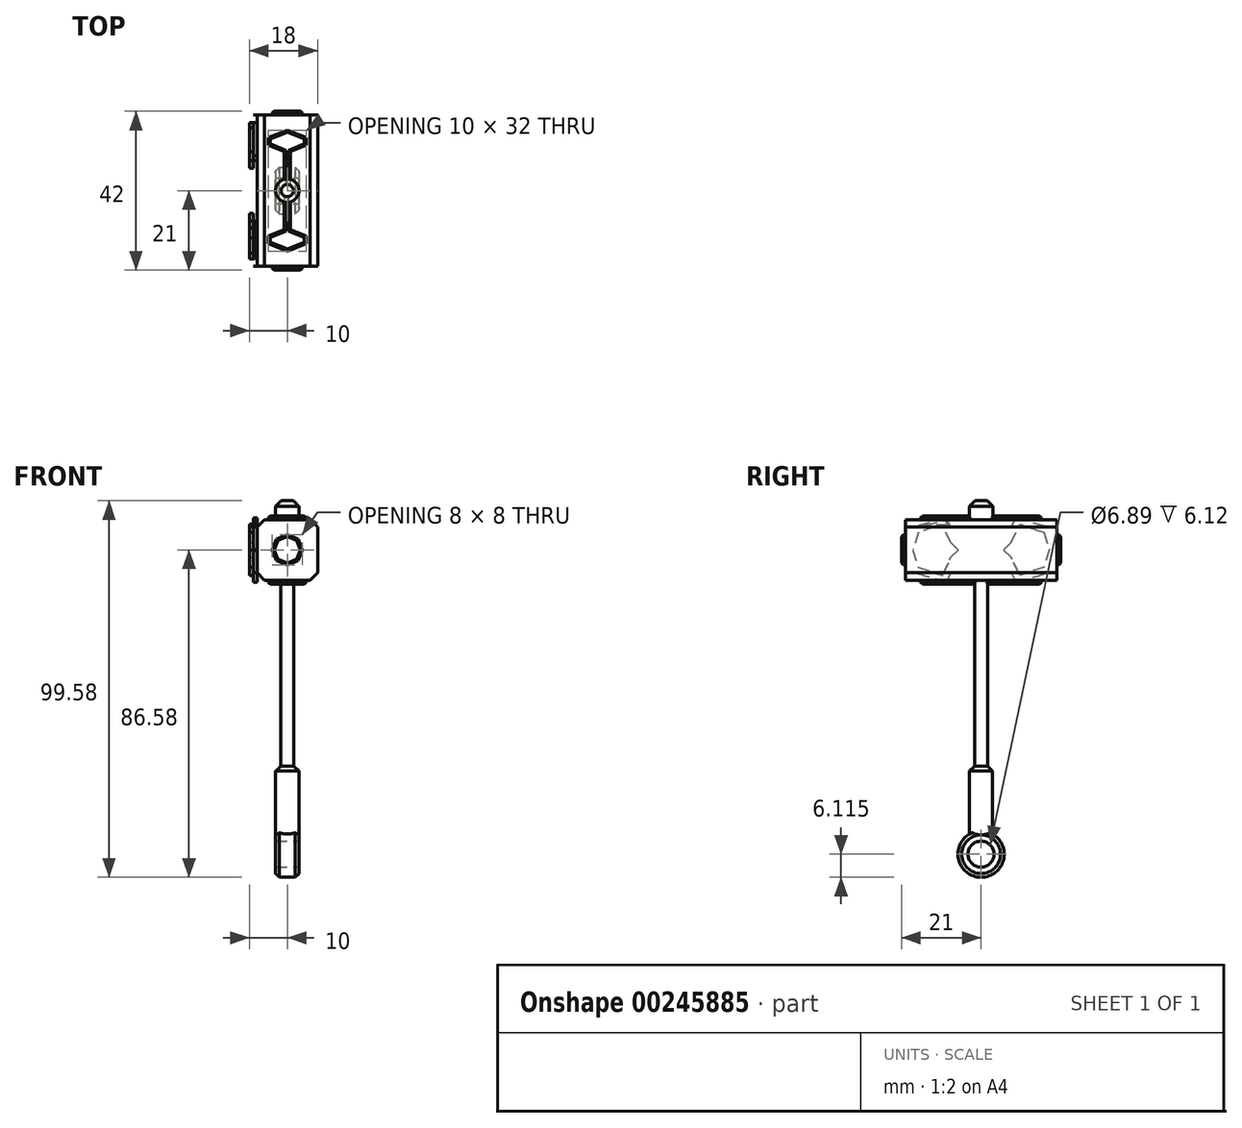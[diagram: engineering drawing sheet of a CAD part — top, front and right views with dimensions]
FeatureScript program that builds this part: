
annotation { "Feature Type Name" : "Feature", "Feature Type Description" : "" }
export const myFeature = defineFeature(function(context is Context, id is Id, definition is map)
    precondition{}
    {
        {
            var Q0;
            Q0=qCreatedBy(makeId("Right.planeOp"),FACE);
            var sketch = newSketch(context, id + "F0", { "sketchPlane" : qUnion([Q0])});
            skLineSegment(sketch, "E0", {"start": v(0, 0) * mm, "end": v(25, 0) * mm});
            skLineSegment(sketch, "E1", {"start": v(25, 0) * mm, "end": v(25, 8) * mm});
            skLineSegment(sketch, "E2", {"start": v(25, 8) * mm, "end": v(0, 8) * mm});
            skLineSegment(sketch, "E3", {"start": v(0, 8) * mm, "end": v(-25, 8) * mm});
            skLineSegment(sketch, "E4", {"start": v(-25, 8) * mm, "end": v(-25, 0) * mm});
            skLineSegment(sketch, "E5", {"start": v(-25, 0) * mm, "end": v(0, 0) * mm});
            skLineSegment(sketch, "E6", {"start": v(25, 0) * mm, "end": v(25, -8) * mm});
            skLineSegment(sketch, "E7", {"start": v(25, -8) * mm, "end": v(-25, -8) * mm});
            skLineSegment(sketch, "E8", {"start": v(-25, -8) * mm, "end": v(-25, 0) * mm});
            skSolve(sketch);
        }
        {
            var Q0;
            Q0=makeQuery(id+"F0.imprint","IMPRINT",FACE,{"disambiguationData":[TD([[makeQuery(id+"F0.imprint","IMPRINT",EDGE,{"derivedFrom":sQuery(id+"F0.wireOp",EDGE,"E0")}),1.0]])]});
            var Q1;
            Q1=makeQuery(id+"F0.imprint","IMPRINT",FACE,{"disambiguationData":[TD([[makeQuery(id+"F0.imprint","IMPRINT",EDGE,{"derivedFrom":sQuery(id+"F0.wireOp",EDGE,"E0")}),-1.0]])]});
            extrude(context, id + "F1", {"entities" : qUnion([Q0, Q1]), "oppositeDirection" : true, "depth" : 8 * mm});
        }
        {
            var Q0;
            Q0=makeQuery(id+"F1.opExtrude","CAP_FACE",FACE,{"disambiguationData":[OSD([sQuery(id+"F0.wireOp",EDGE,"E1"),sQuery(id+"F0.wireOp",EDGE,"E2"),sQuery(id+"F0.wireOp",EDGE,"E3"),sQuery(id+"F0.wireOp",EDGE,"E4"),sQuery(id+"F0.wireOp",EDGE,"E6"),sQuery(id+"F0.wireOp",EDGE,"E7"),sQuery(id+"F0.wireOp",EDGE,"E8")])],"isStart":true});
            extrude(context, id + "F2", {"entities" : qUnion([Q0]), "operationType" : NewBodyOperationType.ADD, "depth" : 8 * mm});
        }
        {
            var Q0;
            {var subQ0=sQuery(id+"F0.wireOp",EDGE,"E8");var subQ1=sQuery(id+"F0.wireOp",EDGE,"E4");Q0=makeQuery(id+"F2.boolean.opBoolean","MERGE",FACE,{"derivedFrom":[makeQuery(id+"F1.opExtrude","SWEPT_FACE",FACE,{"disambiguationData":[OSD([subQ1,subQ0])]}),makeQuery(id+"F2.opExtrude","SWEPT_FACE",FACE,{"disambiguationData":[OSD([subQ1,subQ0])]})]});}
            extrude(context, id + "F3", {"entities" : qUnion([Q0]), "operationType" : NewBodyOperationType.REMOVE, "oppositeDirection" : true, "depth" : 5 * mm});
        }
        {
            var Q0;
            {var subQ0=sQuery(id+"F0.wireOp",EDGE,"E6");var subQ1=sQuery(id+"F0.wireOp",EDGE,"E1");Q0=makeQuery(id+"F2.boolean.opBoolean","MERGE",FACE,{"derivedFrom":[makeQuery(id+"F1.opExtrude","SWEPT_FACE",FACE,{"disambiguationData":[OSD([subQ1,subQ0])]}),makeQuery(id+"F2.opExtrude","SWEPT_FACE",FACE,{"disambiguationData":[OSD([subQ1,subQ0])]})]});}
            extrude(context, id + "F4", {"entities" : qUnion([Q0]), "operationType" : NewBodyOperationType.REMOVE, "oppositeDirection" : true, "depth" : 5 * mm});
        }
        {
            var Q0;
            Q0=makeQuery(id+"F1.opExtrude","CAP_EDGE",EDGE,{"disambiguationData":[OSD([sQuery(id+"F0.wireOp",EDGE,"E2"),sQuery(id+"F0.wireOp",EDGE,"E3")])],"isStart":false});
            var Q1;
            Q1=makeQuery(id+"F4.boolean.opBoolean","COPY",EDGE,{"derivedFrom":makeQuery(id+"F4.opExtrude","CAP_EDGE",EDGE,{"disambiguationData":[OSD([sQuery(id+"F0.wireOp",EDGE,"E1"),sQuery(id+"F0.wireOp",EDGE,"E2")])],"isStart":false})});
            var Q2;
            {var subQ0=sQuery(id+"F0.wireOp",EDGE,"E6");var subQ1=sQuery(id+"F0.wireOp",EDGE,"E1");Q2=makeQuery(id+"F4.boolean.opBoolean","COPY",EDGE,{"derivedFrom":makeQuery(id+"F4.opExtrude","CAP_EDGE",EDGE,{"disambiguationData":[OSD([subQ1,subQ0]),TDD([makeQuery(id+"F1.opExtrude","CAP_EDGE",EDGE,{"disambiguationData":[OSD([subQ1,subQ0])],"isStart":false})])],"isStart":false})});}
            var Q3;
            Q3=makeQuery(id+"F1.opExtrude","CAP_EDGE",EDGE,{"disambiguationData":[OSD([sQuery(id+"F0.wireOp",EDGE,"E7")])],"isStart":false});
            var Q4;
            {var subQ0=sQuery(id+"F0.wireOp",EDGE,"E8");var subQ1=sQuery(id+"F0.wireOp",EDGE,"E4");Q4=makeQuery(id+"F3.boolean.opBoolean","COPY",EDGE,{"derivedFrom":makeQuery(id+"F3.opExtrude","CAP_EDGE",EDGE,{"disambiguationData":[OSD([subQ1,subQ0]),TDD([makeQuery(id+"F1.opExtrude","CAP_EDGE",EDGE,{"disambiguationData":[OSD([subQ1,subQ0])],"isStart":false})])],"isStart":false})});}
            var Q5;
            {var subQ0=sQuery(id+"F0.wireOp",EDGE,"E8");var subQ1=sQuery(id+"F0.wireOp",EDGE,"E4");Q5=makeQuery(id+"F3.boolean.opBoolean","COPY",EDGE,{"derivedFrom":makeQuery(id+"F3.opExtrude","CAP_EDGE",EDGE,{"disambiguationData":[OSD([subQ1,subQ0]),TDD([makeQuery(id+"F2.opExtrude","CAP_EDGE",EDGE,{"disambiguationData":[OSD([subQ1,subQ0])],"isStart":false})])],"isStart":false})});}
            var Q6;
            Q6=makeQuery(id+"F3.boolean.opBoolean","COPY",EDGE,{"derivedFrom":makeQuery(id+"F3.opExtrude","CAP_EDGE",EDGE,{"disambiguationData":[OSD([sQuery(id+"F0.wireOp",EDGE,"E3"),sQuery(id+"F0.wireOp",EDGE,"E4")])],"isStart":false})});
            var Q7;
            Q7=makeQuery(id+"F3.boolean.opBoolean","COPY",EDGE,{"derivedFrom":makeQuery(id+"F3.opExtrude","CAP_EDGE",EDGE,{"disambiguationData":[OSD([sQuery(id+"F0.wireOp",EDGE,"E7"),sQuery(id+"F0.wireOp",EDGE,"E8")])],"isStart":false})});
            var Q8;
            Q8=makeQuery(id+"F2.opExtrude","CAP_EDGE",EDGE,{"disambiguationData":[OSD([sQuery(id+"F0.wireOp",EDGE,"E2"),sQuery(id+"F0.wireOp",EDGE,"E3")])],"isStart":false});
            var Q9;
            Q9=makeQuery(id+"F2.opExtrude","CAP_EDGE",EDGE,{"disambiguationData":[OSD([sQuery(id+"F0.wireOp",EDGE,"E7")])],"isStart":false});
            var Q10;
            Q10=makeQuery(id+"F4.boolean.opBoolean","COPY",EDGE,{"derivedFrom":makeQuery(id+"F4.opExtrude","CAP_EDGE",EDGE,{"disambiguationData":[OSD([sQuery(id+"F0.wireOp",EDGE,"E6"),sQuery(id+"F0.wireOp",EDGE,"E7")])],"isStart":false})});
            var Q11;
            {var subQ0=sQuery(id+"F0.wireOp",EDGE,"E6");var subQ1=sQuery(id+"F0.wireOp",EDGE,"E1");Q11=makeQuery(id+"F4.boolean.opBoolean","COPY",EDGE,{"derivedFrom":makeQuery(id+"F4.opExtrude","CAP_EDGE",EDGE,{"disambiguationData":[OSD([subQ1,subQ0]),TDD([makeQuery(id+"F2.opExtrude","CAP_EDGE",EDGE,{"disambiguationData":[OSD([subQ1,subQ0])],"isStart":false})])],"isStart":false})});}
            chamfer(context, id + "F5", {"entities" : qUnion([Q0, Q1, Q2, Q3, Q4, Q5, Q6, Q7, Q8, Q9, Q10, Q11]), "width" : 2 * mm, "tangentPropagation" : true});
        }
        {
            var Q0;
            {var subQ0=sQuery(id+"F0.wireOp",EDGE,"E3");var subQ1=sQuery(id+"F0.wireOp",EDGE,"E2");Q0=makeQuery(id+"F2.boolean.opBoolean","MERGE",FACE,{"derivedFrom":[makeQuery(id+"F1.opExtrude","SWEPT_FACE",FACE,{"disambiguationData":[OSD([subQ1,subQ0])]}),makeQuery(id+"F2.opExtrude","SWEPT_FACE",FACE,{"disambiguationData":[OSD([subQ1,subQ0])]})]});}
            var sketch = newSketch(context, id + "F6", { "sketchPlane" : qUnion([Q0])});
            skCircle(sketch, "E9", {"center": v(0, 0) * mm, "radius": 1.75 * mm});
            skSolve(sketch);
        }
        {
            var Q0;
            Q0=makeQuery(id+"F6.imprint","IMPRINT",FACE,{"disambiguationData":[TD([[makeQuery(id+"F6.imprint","IMPRINT",EDGE,{"derivedFrom":sQuery(id+"F6.wireOp",EDGE,"E9")}),1.0]])]});
            extrude(context, id + "F7", {"entities" : qUnion([Q0]), "operationType" : NewBodyOperationType.ADD, "oppositeDirection" : true, "depth" : 70 * mm});
        }
        {
            var Q0;
            Q0=makeQuery(id+"F6.imprint","IMPRINT",FACE,{"disambiguationData":[TD([[makeQuery(id+"F6.imprint","IMPRINT",EDGE,{"derivedFrom":sQuery(id+"F6.wireOp",EDGE,"E9")}),1.0]])]});
            extrude(context, id + "F8", {"entities" : qUnion([Q0]), "operationType" : NewBodyOperationType.ADD, "depth" : 5 * mm});
        }
        {
            var Q0;
            Q0=makeQuery(id+"F1.opExtrude","CAP_FACE",FACE,{"disambiguationData":[OSD([sQuery(id+"F0.wireOp",EDGE,"E1"),sQuery(id+"F0.wireOp",EDGE,"E2"),sQuery(id+"F0.wireOp",EDGE,"E3"),sQuery(id+"F0.wireOp",EDGE,"E4"),sQuery(id+"F0.wireOp",EDGE,"E6"),sQuery(id+"F0.wireOp",EDGE,"E7"),sQuery(id+"F0.wireOp",EDGE,"E8")])],"isStart":false});
            var sketch = newSketch(context, id + "F9", { "sketchPlane" : qUnion([Q0])});
            skLineSegment(sketch, "E10", {"start": v(0, 0) * mm, "end": v(-5, 0) * mm});
            skLineSegment(sketch, "E11", {"start": v(6, 2) * mm, "end": v(9.25, 8.5) * mm});
            skLineSegment(sketch, "E12", {"start": v(9.25, 8.5) * mm, "end": v(18, 6) * mm});
            skLineSegment(sketch, "E13", {"start": v(18, 6) * mm, "end": v(20.04, 0) * mm});
            skLineSegment(sketch, "E14", {"start": v(20.04, 0) * mm, "end": v(18, -6) * mm});
            skLineSegment(sketch, "E15.MirrorCS", {"start": v(9.25, -8.5) * mm, "end": v(18, -6) * mm});
            skLineSegment(sketch, "E16.MirrorCS", {"start": v(6, -2) * mm, "end": v(9.25, -8.5) * mm});
            skLineSegment(sketch, "E17.MirrorCS", {"start": v(-6, 2) * mm, "end": v(-9.25, 8.5) * mm});
            skLineSegment(sketch, "E18.MirrorCS", {"start": v(-9.25, 8.5) * mm, "end": v(-18, 6) * mm});
            skLineSegment(sketch, "E19.MirrorCS", {"start": v(-18, 6) * mm, "end": v(-20.04, 0) * mm});
            skLineSegment(sketch, "E20.MirrorCS", {"start": v(-20.04, 0) * mm, "end": v(-18, -6) * mm});
            skLineSegment(sketch, "E21.MirrorCS", {"start": v(-9.25, -8.5) * mm, "end": v(-18, -6) * mm});
            skLineSegment(sketch, "E22.MirrorCS", {"start": v(-6, -2) * mm, "end": v(-9.25, -8.5) * mm});
            skLineSegment(sketch, "E23", {"start": v(-5, -2) * mm, "end": v(-6, -2) * mm});
            skLineSegment(sketch, "E24.bottom", {"start": v(-6, -2) * mm, "end": v(6, -2) * mm});
            skLineSegment(sketch, "E24.top", {"start": v(-6, 2) * mm, "end": v(6, 2) * mm});
            skPoint(sketch, "E25.orphan", {"position": v(5, 0) * mm});
            skPoint(sketch, "E26.orphan", {"position": v(-5, 0) * mm});
            skSolve(sketch);
        }
        {
            var Q0;
            {var subQ0=sQuery(id+"F9.wireOp",EDGE,"E18.MirrorCS");Q0=makeQuery(id+"F9.imprint","IMPRINT",FACE,{"disambiguationData":[TD([[makeQuery(id+"F9.imprint","IMPRINT",EDGE,{"derivedFrom":subQ0}),1.0]])]});}
            var Q1;
            {var subQ18=sQuery(id+"F9.wireOp",EDGE,"E24.top");Q1=makeQuery(id+"F9.imprint","IMPRINT",FACE,{"disambiguationData":[TD([[makeQuery(id+"F9.imprint","IMPRINT",EDGE,{"derivedFrom":subQ18}),-1.0]])]});}
            var Q2;
            Q2=makeQuery(id+"F9.imprint","IMPRINT",FACE,{"disambiguationData":[TD([[makeQuery(id+"F9.imprint","IMPRINT",EDGE,{"derivedFrom":sQuery(id+"F9.wireOp",EDGE,"E19.MirrorCS")}),1.0]])]});
            var Q3;
            {var subQ0=sQuery(id+"F9.wireOp",EDGE,"E21.MirrorCS");Q3=makeQuery(id+"F9.imprint","IMPRINT",FACE,{"disambiguationData":[TD([[makeQuery(id+"F9.imprint","IMPRINT",EDGE,{"derivedFrom":subQ0}),-1.0]])]});}
            var Q4;
            {var subQ0=sQuery(id+"F9.wireOp",EDGE,"E12");Q4=makeQuery(id+"F9.imprint","IMPRINT",FACE,{"disambiguationData":[TD([[makeQuery(id+"F9.imprint","IMPRINT",EDGE,{"derivedFrom":subQ0}),-1.0]])]});}
            var Q5;
            Q5=makeQuery(id+"F9.imprint","IMPRINT",FACE,{"disambiguationData":[TD([[makeQuery(id+"F9.imprint","IMPRINT",EDGE,{"derivedFrom":sQuery(id+"F9.wireOp",EDGE,"E13")}),-1.0]])]});
            var Q6;
            {var subQ0=sQuery(id+"F9.wireOp",EDGE,"E15.MirrorCS");Q6=makeQuery(id+"F9.imprint","IMPRINT",FACE,{"disambiguationData":[TD([[makeQuery(id+"F9.imprint","IMPRINT",EDGE,{"derivedFrom":subQ0}),1.0]])]});}
            extrude(context, id + "F10", {"entities" : qUnion([Q0, Q1, Q2, Q3, Q4, Q5, Q6]), "operationType" : NewBodyOperationType.ADD, "depth" : 1 * mm});
        }
        {
            var Q0;
            Q0=makeQuery(id+"F10.opExtrude","CAP_FACE",FACE,{"disambiguationData":[OSD([sQuery(id+"F9.wireOp",EDGE,"E11"),sQuery(id+"F9.wireOp",EDGE,"E12"),sQuery(id+"F9.wireOp",EDGE,"E13"),sQuery(id+"F9.wireOp",EDGE,"E14"),sQuery(id+"F9.wireOp",EDGE,"E15.MirrorCS"),sQuery(id+"F9.wireOp",EDGE,"E16.MirrorCS"),sQuery(id+"F9.wireOp",EDGE,"E17.MirrorCS"),sQuery(id+"F9.wireOp",EDGE,"E18.MirrorCS"),sQuery(id+"F9.wireOp",EDGE,"E19.MirrorCS"),sQuery(id+"F9.wireOp",EDGE,"E20.MirrorCS"),sQuery(id+"F9.wireOp",EDGE,"E21.MirrorCS"),sQuery(id+"F9.wireOp",EDGE,"E22.MirrorCS"),sQuery(id+"F9.wireOp",EDGE,"E24.bottom"),sQuery(id+"F9.wireOp",EDGE,"E24.top")])],"isStart":false});
            var sketch = newSketch(context, id + "F11", { "sketchPlane" : qUnion([Q0])});
            skLineSegment(sketch, "E27", {"start": v(-6, 2) * mm, "end": v(-8, 2) * mm});
            skLineSegment(sketch, "E28", {"start": v(-6, -2) * mm, "end": v(-8, -2) * mm});
            skLineSegment(sketch, "E29", {"start": v(-9.25, -8.5) * mm, "end": v(-10.23, -6.75) * mm});
            skLineSegment(sketch, "E30", {"start": v(-18, -6) * mm, "end": v(-16.56, -4.6) * mm});
            skLineSegment(sketch, "E31", {"start": v(-20.04, 0) * mm, "end": v(-18.04, 0) * mm});
            skLineSegment(sketch, "E32.MirrorCS", {"start": v(-9.25, 8.5) * mm, "end": v(-10.23, 6.75) * mm});
            skLineSegment(sketch, "E33.MirrorCS", {"start": v(-18, 6) * mm, "end": v(-16.56, 4.6) * mm});
            skLineSegment(sketch, "E34.MirrorCS", {"start": v(9.25, 8.5) * mm, "end": v(10.23, 6.75) * mm});
            skLineSegment(sketch, "E35.MirrorCS", {"start": v(6, 2) * mm, "end": v(8, 2) * mm});
            skLineSegment(sketch, "E36.MirrorCS", {"start": v(6, -2) * mm, "end": v(8, -2) * mm});
            skLineSegment(sketch, "E37.MirrorCS", {"start": v(9.25, -8.5) * mm, "end": v(10.23, -6.75) * mm});
            skLineSegment(sketch, "E38.MirrorCS", {"start": v(18, -6) * mm, "end": v(16.56, -4.6) * mm});
            skLineSegment(sketch, "E39.MirrorCS", {"start": v(20.04, 0) * mm, "end": v(18.04, 0) * mm});
            skLineSegment(sketch, "E40.MirrorCS", {"start": v(18, 6) * mm, "end": v(16.56, 4.6) * mm});
            skLineSegment(sketch, "E41", {"start": v(-8, 2) * mm, "end": v(-10.23, 6.75) * mm});
            skLineSegment(sketch, "E42", {"start": v(-10.23, 6.75) * mm, "end": v(-16.56, 4.6) * mm});
            skLineSegment(sketch, "E43", {"start": v(-16.56, 4.6) * mm, "end": v(-18.04, 0) * mm});
            skLineSegment(sketch, "E44", {"start": v(-18.04, 0) * mm, "end": v(-16.56, -4.6) * mm});
            skLineSegment(sketch, "E45", {"start": v(-16.56, -4.6) * mm, "end": v(-10.23, -6.75) * mm});
            skLineSegment(sketch, "E46", {"start": v(-10.23, -6.75) * mm, "end": v(-8, -2) * mm});
            skLineSegment(sketch, "E47", {"start": v(-8, 2) * mm, "end": v(-5.98, 0) * mm});
            skLineSegment(sketch, "E48", {"start": v(-5.98, 0) * mm, "end": v(-8, -2) * mm});
            skLineSegment(sketch, "E49.MirrorCS", {"start": v(5.98, 0) * mm, "end": v(8, -2) * mm});
            skLineSegment(sketch, "E50.MirrorCS", {"start": v(8, 2) * mm, "end": v(5.98, 0) * mm});
            skLineSegment(sketch, "E51.MirrorCS", {"start": v(8, 2) * mm, "end": v(10.23, 6.75) * mm});
            skLineSegment(sketch, "E52.MirrorCS", {"start": v(10.23, 6.75) * mm, "end": v(16.56, 4.6) * mm});
            skLineSegment(sketch, "E53.MirrorCS", {"start": v(16.56, 4.6) * mm, "end": v(18.04, 0) * mm});
            skLineSegment(sketch, "E54.MirrorCS", {"start": v(18.04, 0) * mm, "end": v(16.56, -4.6) * mm});
            skLineSegment(sketch, "E55.MirrorCS", {"start": v(16.56, -4.6) * mm, "end": v(10.23, -6.75) * mm});
            skLineSegment(sketch, "E56.MirrorCS", {"start": v(10.23, -6.75) * mm, "end": v(8, -2) * mm});
            skSolve(sketch);
        }
        {
            var Q0;
            Q0=makeQuery(id+"F11.imprint","IMPRINT",FACE,{"disambiguationData":[TD([[makeQuery(id+"F11.imprint","IMPRINT",EDGE,{"derivedFrom":sQuery(id+"F11.wireOp",EDGE,"E41")}),1.0]])]});
            var Q1;
            Q1=makeQuery(id+"F11.imprint","IMPRINT",FACE,{"disambiguationData":[TD([[makeQuery(id+"F11.imprint","IMPRINT",EDGE,{"derivedFrom":sQuery(id+"F11.wireOp",EDGE,"E49.MirrorCS")}),1.0]])]});
            extrude(context, id + "F12", {"entities" : qUnion([Q0, Q1]), "operationType" : NewBodyOperationType.ADD, "depth" : 1 * mm});
        }
        {
            var Q0;
            Q0=makeQuery(id+"F10.opExtrude","CAP_EDGE",EDGE,{"disambiguationData":[OSD([sQuery(id+"F9.wireOp",EDGE,"E18.MirrorCS")])],"isStart":false});
            var Q1;
            Q1=makeQuery(id+"F12.opExtrude","CAP_EDGE",EDGE,{"disambiguationData":[OSD([sQuery(id+"F11.wireOp",EDGE,"E42")])],"isStart":false});
            var Q2;
            Q2=makeQuery(id+"F10.opExtrude","CAP_EDGE",EDGE,{"disambiguationData":[OSD([sQuery(id+"F9.wireOp",EDGE,"E19.MirrorCS")])],"isStart":false});
            var Q3;
            Q3=makeQuery(id+"F10.opExtrude","CAP_EDGE",EDGE,{"disambiguationData":[OSD([sQuery(id+"F9.wireOp",EDGE,"E20.MirrorCS")])],"isStart":false});
            var Q4;
            Q4=makeQuery(id+"F10.opExtrude","CAP_EDGE",EDGE,{"disambiguationData":[OSD([sQuery(id+"F9.wireOp",EDGE,"E21.MirrorCS")])],"isStart":false});
            var Q5;
            Q5=makeQuery(id+"F10.opExtrude","CAP_EDGE",EDGE,{"disambiguationData":[OSD([sQuery(id+"F9.wireOp",EDGE,"E22.MirrorCS")])],"isStart":false});
            var Q6;
            Q6=makeQuery(id+"F12.opExtrude","CAP_EDGE",EDGE,{"disambiguationData":[OSD([sQuery(id+"F11.wireOp",EDGE,"E46")])],"isStart":false});
            var Q7;
            Q7=makeQuery(id+"F12.opExtrude","CAP_EDGE",EDGE,{"disambiguationData":[OSD([sQuery(id+"F11.wireOp",EDGE,"E45")])],"isStart":false});
            var Q8;
            Q8=makeQuery(id+"F12.opExtrude","CAP_EDGE",EDGE,{"disambiguationData":[OSD([sQuery(id+"F11.wireOp",EDGE,"E44")])],"isStart":false});
            var Q9;
            Q9=makeQuery(id+"F12.opExtrude","CAP_EDGE",EDGE,{"disambiguationData":[OSD([sQuery(id+"F11.wireOp",EDGE,"E43")])],"isStart":false});
            var Q10;
            Q10=makeQuery(id+"F12.opExtrude","CAP_EDGE",EDGE,{"disambiguationData":[OSD([sQuery(id+"F11.wireOp",EDGE,"E41")])],"isStart":false});
            var Q11;
            Q11=makeQuery(id+"F12.opExtrude","CAP_EDGE",EDGE,{"disambiguationData":[OSD([sQuery(id+"F11.wireOp",EDGE,"E47")])],"isStart":false});
            var Q12;
            Q12=makeQuery(id+"F12.opExtrude","CAP_EDGE",EDGE,{"disambiguationData":[OSD([sQuery(id+"F11.wireOp",EDGE,"E48")])],"isStart":false});
            var Q13;
            Q13=makeQuery(id+"F10.opExtrude","CAP_EDGE",EDGE,{"disambiguationData":[OSD([sQuery(id+"F9.wireOp",EDGE,"E24.top")])],"isStart":false});
            var Q14;
            Q14=makeQuery(id+"F10.opExtrude","CAP_EDGE",EDGE,{"disambiguationData":[OSD([sQuery(id+"F9.wireOp",EDGE,"E17.MirrorCS")])],"isStart":false});
            var Q15;
            Q15=makeQuery(id+"F10.opExtrude","CAP_FACE",FACE,{"disambiguationData":[OSD([sQuery(id+"F9.wireOp",EDGE,"E11"),sQuery(id+"F9.wireOp",EDGE,"E12"),sQuery(id+"F9.wireOp",EDGE,"E13"),sQuery(id+"F9.wireOp",EDGE,"E14"),sQuery(id+"F9.wireOp",EDGE,"E15.MirrorCS"),sQuery(id+"F9.wireOp",EDGE,"E16.MirrorCS"),sQuery(id+"F9.wireOp",EDGE,"E17.MirrorCS"),sQuery(id+"F9.wireOp",EDGE,"E18.MirrorCS"),sQuery(id+"F9.wireOp",EDGE,"E19.MirrorCS"),sQuery(id+"F9.wireOp",EDGE,"E20.MirrorCS"),sQuery(id+"F9.wireOp",EDGE,"E21.MirrorCS"),sQuery(id+"F9.wireOp",EDGE,"E22.MirrorCS"),sQuery(id+"F9.wireOp",EDGE,"E24.bottom"),sQuery(id+"F9.wireOp",EDGE,"E24.top")])],"isStart":false});
            chamfer(context, id + "F13", {"entities" : qUnion([Q0, Q1, Q2, Q3, Q4, Q5, Q6, Q7, Q8, Q9, Q10, Q11, Q12, Q13, Q14, Q15]), "width" : 0.5 * mm, "tangentPropagation" : true});
        }
        {
            var Q0;
            Q0=makeQuery(id+"F8.opExtrude","CAP_FACE",FACE,{"disambiguationData":[OSD([sQuery(id+"F6.wireOp",EDGE,"E9")])],"isStart":false});
            var sketch = newSketch(context, id + "F14", { "sketchPlane" : qUnion([Q0])});
            skCircle(sketch, "E57", {"center": v(0, 0) * mm, "radius": 3.1 * mm});
            skSolve(sketch);
        }
        {
            var Q0;
            Q0=makeQuery(id+"F14.imprint","IMPRINT",FACE,{"disambiguationData":[TD([[makeQuery(id+"F14.imprint","IMPRINT",EDGE,{"derivedFrom":sQuery(id+"F14.wireOp",EDGE,"E57")}),1.0]])]});
            extrude(context, id + "F15", {"entities" : qUnion([Q0]), "operationType" : NewBodyOperationType.ADD, "oppositeDirection" : true, "depth" : 5 * mm});
        }
        {
            var Q0;
            Q0=makeQuery(id+"F7.opExtrude","CAP_FACE",FACE,{"disambiguationData":[OSD([sQuery(id+"F6.wireOp",EDGE,"E9")])],"isStart":false});
            var sketch = newSketch(context, id + "F16", { "sketchPlane" : qUnion([Q0])});
            skCircle(sketch, "E58", {"center": v(0, 0) * mm, "radius": 3.06 * mm});
            skSolve(sketch);
        }
        {
            var Q0;
            Q0=makeQuery(id+"F16.imprint","IMPRINT",FACE,{"disambiguationData":[TD([[makeQuery(id+"F16.imprint","IMPRINT",EDGE,{"derivedFrom":sQuery(id+"F16.wireOp",EDGE,"E58")}),1.0]])]});
            extrude(context, id + "F17", {"entities" : qUnion([Q0]), "operationType" : NewBodyOperationType.ADD, "oppositeDirection" : true, "depth" : 5 * mm});
        }
        {
            var Q0;
            {var subQ0=sQuery(id+"F6.wireOp",EDGE,"E9");Q0=makeQuery(id+"F17.boolean.opBoolean","MERGE",FACE,{"derivedFrom":[makeQuery(id+"F7.opExtrude","CAP_FACE",FACE,{"disambiguationData":[OSD([subQ0])],"isStart":false}),makeQuery(id+"F17.opExtrude","CAP_FACE",FACE,{"disambiguationData":[OSD([subQ0,sQuery(id+"F16.wireOp",EDGE,"E58")])],"isStart":true})]});}
            extrude(context, id + "F18", {"entities" : qUnion([Q0]), "operationType" : NewBodyOperationType.ADD, "depth" : 15 * mm});
        }
        {
            var Q0;
            Q0=makeQuery(id+"F17.opExtrude","CAP_EDGE",EDGE,{"disambiguationData":[OSD([sQuery(id+"F16.wireOp",EDGE,"E58")])],"isStart":false});
            var Q1;
            Q1=makeQuery(id+"F18.opExtrude","CAP_EDGE",EDGE,{"disambiguationData":[OSD([sQuery(id+"F16.wireOp",EDGE,"E58")])],"isStart":false});
            var Q2;
            {var subQ0=sQuery(id+"F6.wireOp",EDGE,"E9");Q2=makeQuery(id+"F15.boolean.opBoolean","MERGE",FACE,{"derivedFrom":[makeQuery(id+"F8.opExtrude","CAP_FACE",FACE,{"disambiguationData":[OSD([subQ0])],"isStart":false}),makeQuery(id+"F15.opExtrude","CAP_FACE",FACE,{"disambiguationData":[OSD([subQ0,sQuery(id+"F14.wireOp",EDGE,"E57")])],"isStart":true})]});}
            var Q3;
            Q3=makeQuery(id+"F15.opExtrude","CAP_EDGE",EDGE,{"disambiguationData":[OSD([sQuery(id+"F14.wireOp",EDGE,"E57")])],"isStart":false});
            chamfer(context, id + "F19", {"entities" : qUnion([Q0, Q1, Q2, Q3]), "width" : 1.5 * mm, "tangentPropagation" : true});
        }
        {
            var Q0;
            Q0=qCreatedBy(makeId("Front.planeOp"),FACE);
            var sketch = newSketch(context, id + "F20", { "sketchPlane" : qUnion([Q0])});
            skLineSegment(sketch, "E59", {"start": v(0, -74.34) * mm, "end": v(3.06, -74.34) * mm});
            skLineSegment(sketch, "E60", {"start": v(3.06, -74.34) * mm, "end": v(3.06, -80.46) * mm});
            skLineSegment(sketch, "E61", {"start": v(3.06, -80.46) * mm, "end": v(-3.06, -80.46) * mm});
            skLineSegment(sketch, "E62", {"start": v(-3.06, -80.46) * mm, "end": v(-3.06, -74.34) * mm});
            skLineSegment(sketch, "E63", {"start": v(-3.06, -74.34) * mm, "end": v(0, -74.34) * mm});
            skLineSegment(sketch, "E64", {"start": v(0, -77.02) * mm, "end": v(3.06, -77.02) * mm});
            skLineSegment(sketch, "E65", {"start": v(3.06, -77.02) * mm, "end": v(-3.06, -77.02) * mm});
            skPoint(sketch, "E65.endSnap0", {"position": v(-3.06, -77.4) * mm});
            skLineSegment(sketch, "E66", {"start": v(0, -78.8) * mm, "end": v(-3.06, -78.8) * mm});
            skLineSegment(sketch, "E67", {"start": v(-3.06, -78.8) * mm, "end": v(3.06, -78.8) * mm});
            skSolve(sketch);
        }
        {
            var Q0;
            {var subQ5=sQuery(id+"F20.wireOp",EDGE,"E59");Q0=makeQuery(id+"F20.imprint","IMPRINT",FACE,{"disambiguationData":[TD([[makeQuery(id+"F20.imprint","IMPRINT",EDGE,{"derivedFrom":subQ5}),-1.0]])]});}
            var Q1;
            Q1=sQuery(id+"F20.wireOp",EDGE,"E61");
            revolve(context, id + "F21", {"operationType" : NewBodyOperationType.ADD, "entities" : qUnion([Q0]), "axis" : qUnion([Q1]), "revolveType" : RevolveType.FULL});
        }
        {
            var Q0;
            Q0=makeQuery(id+"F21.opRevolve","SWEPT_EDGE",EDGE,{"disambiguationData":[OSD([sQuery(id+"F20.wireOp",EDGE,"E62"),sQuery(id+"F20.wireOp",EDGE,"E63")])]});
            var Q1;
            Q1=makeQuery(id+"F21.opRevolve","SWEPT_EDGE",EDGE,{"disambiguationData":[OSD([sQuery(id+"F20.wireOp",EDGE,"E59"),sQuery(id+"F20.wireOp",EDGE,"E60")])]});
            chamfer(context, id + "F22", {"entities" : qUnion([Q0, Q1]), "width" : 1 * mm, "tangentPropagation" : true});
        }
        {
            var Q0;
            Q0=makeQuery(id+"F1.opExtrude","SWEPT_BODY",BODY,{"disambiguationData":[OSD([sQuery(id+"F0.wireOp",EDGE,"E1"),sQuery(id+"F0.wireOp",EDGE,"E2"),sQuery(id+"F0.wireOp",EDGE,"E3"),sQuery(id+"F0.wireOp",EDGE,"E4"),sQuery(id+"F0.wireOp",EDGE,"E6"),sQuery(id+"F0.wireOp",EDGE,"E7"),sQuery(id+"F0.wireOp",EDGE,"E8")])]});
            var Q1;
            Q1=qCreatedBy(makeId("Right.planeOp"),FACE);
            mirror(context, id + "F23", {"operationType" : NewBodyOperationType.ADD, "entities" : qUnion([Q0]), "mirrorPlane" : qUnion([Q1])});
        }
        {
            var Q0;
            Q0=makeQuery(id+"F3.boolean.opBoolean","COPY",FACE,{"derivedFrom":makeQuery(id+"F3.opExtrude","CAP_FACE",FACE,{"disambiguationData":[OSD([sQuery(id+"F0.wireOp",EDGE,"E4"),sQuery(id+"F0.wireOp",EDGE,"E8")])],"isStart":false})});
            var sketch = newSketch(context, id + "F24", { "sketchPlane" : qUnion([Q0])});
            skLineSegment(sketch, "E68", {"start": v(0, 0) * mm, "end": v(0, 4) * mm});
            skLineSegment(sketch, "E69", {"start": v(0, 4) * mm, "end": v(0, -4) * mm});
            skLineSegment(sketch, "E70", {"start": v(0, 0) * mm, "end": v(4, 0) * mm});
            skLineSegment(sketch, "E71", {"start": v(4, 0) * mm, "end": v(-4, 0) * mm});
            skLineSegment(sketch, "E72", {"start": v(0, 0) * mm, "end": v(-2.83, -2.83) * mm});
            skLineSegment(sketch, "E73", {"start": v(-2.83, -2.83) * mm, "end": v(0, 0) * mm});
            skLineSegment(sketch, "E74", {"start": v(-2.83, -2.83) * mm, "end": v(2.83, 2.83) * mm});
            skPoint(sketch, "E75.orphan", {"position": v(-3, -3) * mm});
            skPoint(sketch, "E76.orphan", {"position": v(-6, -6) * mm});
            skLineSegment(sketch, "E77.MirrorCS", {"start": v(-2.83, 2.83) * mm, "end": v(2.83, -2.83) * mm});
            skLineSegment(sketch, "E78", {"start": v(-2.83, 2.83) * mm, "end": v(0, 4) * mm});
            skLineSegment(sketch, "E79", {"start": v(0, 4) * mm, "end": v(2.83, 2.83) * mm});
            skLineSegment(sketch, "E80", {"start": v(2.83, 2.83) * mm, "end": v(4, 0) * mm});
            skLineSegment(sketch, "E81", {"start": v(4, 0) * mm, "end": v(2.83, -2.83) * mm});
            skLineSegment(sketch, "E82", {"start": v(2.83, -2.83) * mm, "end": v(0, -4) * mm});
            skLineSegment(sketch, "E83", {"start": v(0, -4) * mm, "end": v(-2.83, -2.83) * mm});
            skLineSegment(sketch, "E84", {"start": v(-2.83, -2.83) * mm, "end": v(-4, 0) * mm});
            skLineSegment(sketch, "E85", {"start": v(-4, 0) * mm, "end": v(-2.83, 2.83) * mm});
            skSolve(sketch);
        }
        {
            var Q0;
            {var subQ0=sQuery(id+"F24.wireOp",EDGE,"E85");Q0=makeQuery(id+"F24.imprint","IMPRINT",FACE,{"disambiguationData":[TD([[makeQuery(id+"F24.imprint","IMPRINT",EDGE,{"derivedFrom":subQ0}),-1.0]])]});}
            var Q1;
            {var subQ0=sQuery(id+"F24.wireOp",EDGE,"E78");Q1=makeQuery(id+"F24.imprint","IMPRINT",FACE,{"disambiguationData":[TD([[makeQuery(id+"F24.imprint","IMPRINT",EDGE,{"derivedFrom":subQ0}),-1.0]])]});}
            var Q2;
            {var subQ0=sQuery(id+"F24.wireOp",EDGE,"E79");Q2=makeQuery(id+"F24.imprint","IMPRINT",FACE,{"disambiguationData":[TD([[makeQuery(id+"F24.imprint","IMPRINT",EDGE,{"derivedFrom":subQ0}),-1.0]])]});}
            var Q3;
            {var subQ0=sQuery(id+"F24.wireOp",EDGE,"E80");Q3=makeQuery(id+"F24.imprint","IMPRINT",FACE,{"disambiguationData":[TD([[makeQuery(id+"F24.imprint","IMPRINT",EDGE,{"derivedFrom":subQ0}),-1.0]])]});}
            var Q4;
            {var subQ0=sQuery(id+"F24.wireOp",EDGE,"E81");Q4=makeQuery(id+"F24.imprint","IMPRINT",FACE,{"disambiguationData":[TD([[makeQuery(id+"F24.imprint","IMPRINT",EDGE,{"derivedFrom":subQ0}),-1.0]])]});}
            var Q5;
            {var subQ0=sQuery(id+"F24.wireOp",EDGE,"E82");Q5=makeQuery(id+"F24.imprint","IMPRINT",FACE,{"disambiguationData":[TD([[makeQuery(id+"F24.imprint","IMPRINT",EDGE,{"derivedFrom":subQ0}),-1.0]])]});}
            var Q6;
            {var subQ0=sQuery(id+"F24.wireOp",EDGE,"E83");Q6=makeQuery(id+"F24.imprint","IMPRINT",FACE,{"disambiguationData":[TD([[makeQuery(id+"F24.imprint","IMPRINT",EDGE,{"derivedFrom":subQ0}),-1.0]])]});}
            var Q7;
            {var subQ0=sQuery(id+"F24.wireOp",EDGE,"E84");Q7=makeQuery(id+"F24.imprint","IMPRINT",FACE,{"disambiguationData":[TD([[makeQuery(id+"F24.imprint","IMPRINT",EDGE,{"derivedFrom":subQ0}),-1.0]])]});}
            extrude(context, id + "F25", {"entities" : qUnion([Q0, Q1, Q2, Q3, Q4, Q5, Q6, Q7]), "operationType" : NewBodyOperationType.ADD, "depth" : 1 * mm});
        }
        {
            var Q0;
            Q0=makeQuery(id+"F25.opExtrude","CAP_FACE",FACE,{"disambiguationData":[OSD([sQuery(id+"F24.wireOp",EDGE,"E78"),sQuery(id+"F24.wireOp",EDGE,"E79"),sQuery(id+"F24.wireOp",EDGE,"E80"),sQuery(id+"F24.wireOp",EDGE,"E81"),sQuery(id+"F24.wireOp",EDGE,"E82"),sQuery(id+"F24.wireOp",EDGE,"E83"),sQuery(id+"F24.wireOp",EDGE,"E84"),sQuery(id+"F24.wireOp",EDGE,"E85")])],"isStart":false});
            chamfer(context, id + "F26", {"entities" : qUnion([Q0]), "width" : 0.5 * mm, "tangentPropagation" : true});
        }
        {
            var Q0;
            Q0=makeQuery(id+"F1.opExtrude","SWEPT_BODY",BODY,{"disambiguationData":[OSD([sQuery(id+"F0.wireOp",EDGE,"E1"),sQuery(id+"F0.wireOp",EDGE,"E2"),sQuery(id+"F0.wireOp",EDGE,"E3"),sQuery(id+"F0.wireOp",EDGE,"E4"),sQuery(id+"F0.wireOp",EDGE,"E6"),sQuery(id+"F0.wireOp",EDGE,"E7"),sQuery(id+"F0.wireOp",EDGE,"E8")])]});
            var Q1;
            Q1=qCreatedBy(makeId("Front.planeOp"),FACE);
            mirror(context, id + "F27", {"operationType" : NewBodyOperationType.ADD, "entities" : qUnion([Q0]), "mirrorPlane" : qUnion([Q1])});
        }
        {
            var Q0;
            {var subQ0=sQuery(id+"F0.wireOp",EDGE,"E7");Q0=makeQuery(id+"F2.boolean.opBoolean","MERGE",FACE,{"derivedFrom":[makeQuery(id+"F1.opExtrude","SWEPT_FACE",FACE,{"disambiguationData":[OSD([subQ0])]}),makeQuery(id+"F2.opExtrude","SWEPT_FACE",FACE,{"disambiguationData":[OSD([subQ0])]})]});}
            var sketch = newSketch(context, id + "F28", { "sketchPlane" : qUnion([Q0])});
            skLineSegment(sketch, "E86", {"start": v(5, -12) * mm, "end": v(0.82, -10.33) * mm});
            skLineSegment(sketch, "E87.MirrorCS", {"start": v(-5, -12) * mm, "end": v(-0.82, -10.33) * mm});
            skLineSegment(sketch, "E88", {"start": v(5, -12) * mm, "end": v(5, -14) * mm});
            skLineSegment(sketch, "E89", {"start": v(5, -14) * mm, "end": v(0, -16) * mm});
            skLineSegment(sketch, "E90", {"start": v(0, -16) * mm, "end": v(-5, -14) * mm});
            skLineSegment(sketch, "E91", {"start": v(-5, -14) * mm, "end": v(-5, -12) * mm});
            skPoint(sketch, "E92.start.orphan", {"position": v(0, 0) * mm});
            skLineSegment(sketch, "E93.MirrorCS", {"start": v(5, 12) * mm, "end": v(0.82, 10.33) * mm});
            skLineSegment(sketch, "E94.MirrorCS", {"start": v(-5, 12) * mm, "end": v(-0.82, 10.33) * mm});
            skLineSegment(sketch, "E95.MirrorCS", {"start": v(-5, 14) * mm, "end": v(-5, 12) * mm});
            skLineSegment(sketch, "E96.MirrorCS", {"start": v(0, 16) * mm, "end": v(-5, 14) * mm});
            skLineSegment(sketch, "E97.MirrorCS", {"start": v(5, 14) * mm, "end": v(0, 16) * mm});
            skLineSegment(sketch, "E98.MirrorCS", {"start": v(5, 12) * mm, "end": v(5, 14) * mm});
            skLineSegment(sketch, "E99", {"start": v(0.82, 10.33) * mm, "end": v(0.82, -10.33) * mm});
            skPoint(sketch, "E99.endSnap0", {"position": v(2.5, -11) * mm});
            skLineSegment(sketch, "E100", {"start": v(-0.82, -10.33) * mm, "end": v(-0.82, 10.33) * mm});
            skPoint(sketch, "E101.orphan", {"position": v(0, 10) * mm});
            skPoint(sketch, "E102.orphan", {"position": v(0, -10) * mm});
            skPoint(sketch, "E103.orphan", {"position": v(-0.82, -11) * mm});
            skPoint(sketch, "E104.orphan", {"position": v(0.82, -11) * mm});
            skSolve(sketch);
        }
        {
            var Q0;
            Q0 = qSketchRegion(id + "F28", true);
            extrude(context, id + "F29", {"entities" : qUnion([Q0]), "depth" : 1 * mm});
        }
        {
            var Q0;
            Q0=makeQuery(id+"F29.opExtrude","CAP_FACE",FACE,{"disambiguationData":[OSD([sQuery(id+"F28.wireOp",EDGE,"E86"),sQuery(id+"F28.wireOp",EDGE,"E87.MirrorCS"),sQuery(id+"F28.wireOp",EDGE,"E88"),sQuery(id+"F28.wireOp",EDGE,"E89"),sQuery(id+"F28.wireOp",EDGE,"E90"),sQuery(id+"F28.wireOp",EDGE,"E91"),sQuery(id+"F28.wireOp",EDGE,"E94.MirrorCS"),sQuery(id+"F28.wireOp",EDGE,"E95.MirrorCS"),sQuery(id+"F28.wireOp",EDGE,"E96.MirrorCS"),sQuery(id+"F28.wireOp",EDGE,"E97.MirrorCS"),sQuery(id+"F28.wireOp",EDGE,"E98.MirrorCS"),sQuery(id+"F28.wireOp",EDGE,"E93.MirrorCS"),sQuery(id+"F28.wireOp",EDGE,"E99"),sQuery(id+"F28.wireOp",EDGE,"E100")])],"isStart":false});
            chamfer(context, id + "F30", {"entities" : qUnion([Q0]), "width" : 0.5 * mm, "tangentPropagation" : true});
        }
        {
            var Q0;
            Q0=makeQuery(id+"F29.opExtrude","SWEPT_BODY",BODY,{"disambiguationData":[OSD([sQuery(id+"F28.wireOp",EDGE,"E86"),sQuery(id+"F28.wireOp",EDGE,"E87.MirrorCS"),sQuery(id+"F28.wireOp",EDGE,"E88"),sQuery(id+"F28.wireOp",EDGE,"E89"),sQuery(id+"F28.wireOp",EDGE,"E90"),sQuery(id+"F28.wireOp",EDGE,"E91"),sQuery(id+"F28.wireOp",EDGE,"E94.MirrorCS"),sQuery(id+"F28.wireOp",EDGE,"E95.MirrorCS"),sQuery(id+"F28.wireOp",EDGE,"E96.MirrorCS"),sQuery(id+"F28.wireOp",EDGE,"E97.MirrorCS"),sQuery(id+"F28.wireOp",EDGE,"E98.MirrorCS"),sQuery(id+"F28.wireOp",EDGE,"E93.MirrorCS"),sQuery(id+"F28.wireOp",EDGE,"E99"),sQuery(id+"F28.wireOp",EDGE,"E100")])]});
            var Q1;
            Q1=qCreatedBy(makeId("Top.planeOp"),FACE);
            mirror(context, id + "F31", {"operationType" : NewBodyOperationType.ADD, "entities" : qUnion([Q0]), "mirrorPlane" : qUnion([Q1])});
        }
    });
